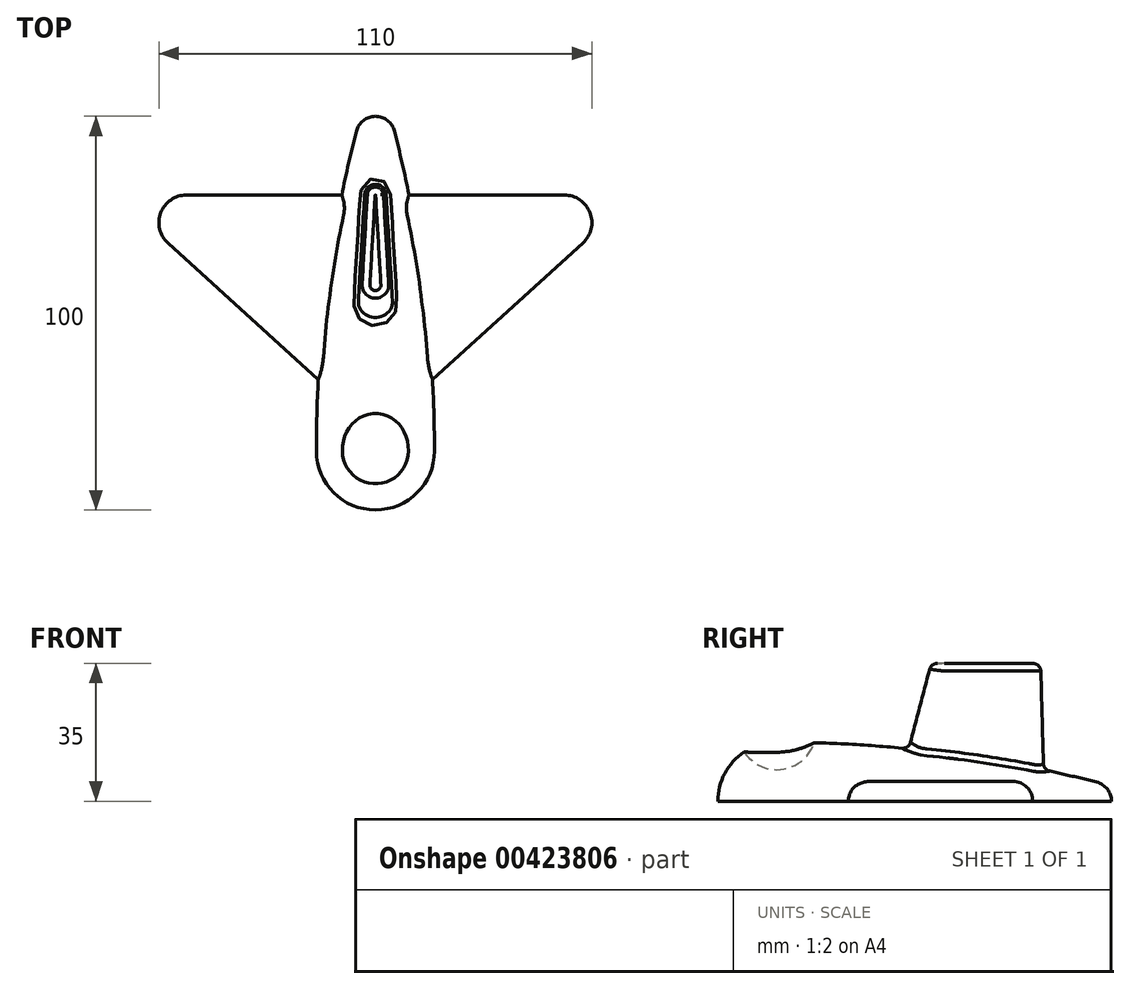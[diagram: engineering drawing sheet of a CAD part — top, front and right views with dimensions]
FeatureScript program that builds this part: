
annotation { "Feature Type Name" : "Feature", "Feature Type Description" : "" }
export const myFeature = defineFeature(function(context is Context, id is Id, definition is map)
    precondition{}
    {
        {
            var Q0;
            Q0=qCreatedBy(makeId("Top.planeOp"),FACE);
            var sketch = newSketch(context, id + "F0", { "sketchPlane" : qUnion([Q0])});
            skArc(sketch, "E0", {"start": v(-15, 0) * mm, "mid": v(-10.6, -10.6) * mm, "end": v(0, -15) * mm});
            skArc(sketch, "E1", {"start": v(0, 85) * mm, "mid": v(-3.07, 83.95) * mm, "end": v(-4.85, 81.23) * mm});
            skLineSegment(sketch, "E2", {"start": v(0, 0) * mm, "end": v(0, 80) * mm});
            skArc(sketch, "E3", {"start": v(-4.85, 81.23) * mm, "mid": v(-12.45, 40.93) * mm, "end": v(-15, 0) * mm});
            skLineSegment(sketch, "E4", {"start": v(0, -15) * mm, "end": v(0, 0) * mm});
            skLineSegment(sketch, "E5.trimOffspring", {"start": v(0, 80) * mm, "end": v(0, 85) * mm});
            skSolve(sketch);
        }
        {
            var Q0;
            Q0=makeQuery(id+"F0.imprint","IMPRINT",FACE,{"disambiguationData":[TD([[makeQuery(id+"F0.imprint","IMPRINT",EDGE,{"derivedFrom":sQuery(id+"F0.wireOp",EDGE,"E0")}),1.0]])]});
            var Q1;
            Q1=sQuery(id+"F0.wireOp",EDGE,"E2");
            revolve(context, id + "F1", {"entities" : qUnion([Q0]), "axis" : qUnion([Q1]), "revolveType" : RevolveType.ONE_DIRECTION, "angle" : 180 * degree});
        }
        {
            var Q0;
            Q0=qCreatedBy(makeId("Right.planeOp"),FACE);
            var sketch = newSketch(context, id + "F2", { "sketchPlane" : qUnion([Q0])});
            skArc(sketch, "E6", {"start": v(-9.34, 14.42) * mm, "mid": v(3.7, 8.71) * mm, "end": v(9.24, 21.83) * mm});
            skLineSegment(sketch, "E7", {"start": v(-9.34, 14.42) * mm, "end": v(9.24, 21.83) * mm});
            skSolve(sketch);
        }
        {
            var Q0;
            Q0 = qSketchRegion(id + "F2", true);
            var Q1;
            Q1=sQuery(id+"F2.wireOp",EDGE,"E7");
            revolve(context, id + "F3", {"operationType" : NewBodyOperationType.REMOVE, "entities" : qUnion([Q0]), "axis" : qUnion([Q1]), "revolveType" : RevolveType.FULL, "oppositeDirection" : true});
        }
        {
            var Q0;
            Q0=qCreatedBy(makeId("Top.planeOp"),FACE);
            var sketch = newSketch(context, id + "F4", { "sketchPlane" : qUnion([Q0])});
            skLineSegment(sketch, "E8", {"start": v(0, 5) * mm, "end": v(0, 65) * mm});
            skLineSegment(sketch, "E9", {"start": v(0, 65) * mm, "end": v(-48, 65) * mm});
            skLineSegment(sketch, "E10", {"start": v(-52.7, 52.82) * mm, "end": v(0, 5) * mm});
            skPoint(sketch, "E11.visualSharp", {"position": v(-66.13, 65) * mm});
            skArc(sketch, "E11.filletArc", {"start": v(-48, 65) * mm, "mid": v(-54.53, 60.52) * mm, "end": v(-52.7, 52.82) * mm});
            skSolve(sketch);
        }
        {
            var Q0;
            Q0=makeQuery(id+"F4.imprint","IMPRINT",FACE,{"disambiguationData":[TD([[makeQuery(id+"F4.imprint","IMPRINT",EDGE,{"derivedFrom":sQuery(id+"F4.wireOp",EDGE,"E8")}),1.0]])]});
            extrude(context, id + "F5", {"entities" : qUnion([Q0]), "depth" : 5 * mm});
        }
        {
            var Q0;
            Q0=makeQuery(id+"F5.opExtrude","CAP_FACE",FACE,{"disambiguationData":[OSD([sQuery(id+"F4.wireOp",EDGE,"E8"),sQuery(id+"F4.wireOp",EDGE,"E9"),sQuery(id+"F4.wireOp",EDGE,"E10"),sQuery(id+"F4.wireOp",EDGE,"E11.filletArc")])],"isStart":false});
            fillet(context, id + "F6", {"entities" : qUnion([Q0]), "radius" : 5 * mm, "tangentPropagation" : true, "allowEdgeOverflow" : false});
        }
        {
            var Q0;
            Q0=makeQuery(id+"F5.opExtrude","SWEPT_BODY",BODY,{"disambiguationData":[OSD([sQuery(id+"F4.wireOp",EDGE,"E8"),sQuery(id+"F4.wireOp",EDGE,"E9"),sQuery(id+"F4.wireOp",EDGE,"E10"),sQuery(id+"F4.wireOp",EDGE,"E11.filletArc")])]});
            var Q1;
            Q1=qCreatedBy(makeId("Right.planeOp"),FACE);
            mirror(context, id + "F7", {"operationType" : NewBodyOperationType.ADD, "entities" : qUnion([Q0]), "mirrorPlane" : qUnion([Q1])});
        }
        {
            var Q0;
            Q0=qCreatedBy(makeId("Top.planeOp"),FACE);
            var sketch = newSketch(context, id + "F8", { "sketchPlane" : qUnion([Q0])});
            skArc(sketch, "E12", {"start": v(3, 65.2) * mm, "mid": v(0, 68) * mm, "end": v(-3, 65.2) * mm});
            skArc(sketch, "E13", {"start": v(-4.99, 35.33) * mm, "mid": v(0, 30) * mm, "end": v(4.99, 35.33) * mm});
            skLineSegment(sketch, "E14", {"start": v(3, 65.2) * mm, "end": v(4.99, 35.33) * mm});
            skLineSegment(sketch, "E15.MirrorCS", {"start": v(-3, 65.2) * mm, "end": v(-4.99, 35.33) * mm});
            skSolve(sketch);
        }
        {
            var Q0;
            Q0=qCreatedBy(makeId("Top.planeOp"),FACE);
            cPlane(context, id + "F9", {"entities" : qUnion([Q0]), "cplaneType" : CPlaneType.OFFSET, "offset" : 35 * mm, "width" : 150 * mm, "height" : 150 * mm});
        }
        {
            var Q0;
            Q0=qCreatedBy(id+"F9.planeOp",FACE);
            var sketch = newSketch(context, id + "F10", { "sketchPlane" : qUnion([Q0])});
            skArc(sketch, "E16", {"start": v(-3.3, 42.7) * mm, "mid": v(0, 39.2) * mm, "end": v(3.3, 42.7) * mm});
            skArc(sketch, "E17", {"start": v(2, 65.12) * mm, "mid": v(0, 67) * mm, "end": v(-2, 65.12) * mm});
            skLineSegment(sketch, "E18", {"start": v(2, 65.12) * mm, "end": v(3.3, 42.7) * mm});
            skLineSegment(sketch, "E19.MirrorCS", {"start": v(-2, 65.12) * mm, "end": v(-3.3, 42.7) * mm});
            skSolve(sketch);
        }
        {
            var Q1;
            Q1 = qSketchRegion(id + "F8", true);
            var Q2;
            Q2=makeQuery(id+"F10.imprint","IMPRINT",FACE,{"disambiguationData":[TD([[makeQuery(id+"F10.imprint","IMPRINT",EDGE,{"derivedFrom":sQuery(id+"F10.wireOp",EDGE,"E16")}),1.0]])]});
            loft(context, id + "F11", {"operationType" : NewBodyOperationType.ADD, "sheetProfilesArray" : [{ "sheetProfileEntities" : qUnion([Q1]) }, { "sheetProfileEntities" : qUnion([Q2]) }]});
        }
        {
            var Q0;
            Q0=makeQuery(id+"F11.opLoft","CAP_FACE",FACE,{"disambiguationData":[OSD([makeQuery(id+"F10.imprint","IMPRINT",FACE,{"disambiguationData":[TD([[makeQuery(id+"F10.imprint","IMPRINT",EDGE,{"derivedFrom":sQuery(id+"F10.wireOp",EDGE,"E16")}),1.0]])]})])],"isStart":true});
            fillet(context, id + "F12", {"entities" : qUnion([Q0]), "radius" : 2 * mm, "tangentPropagation" : true, "allowEdgeOverflow" : false});
        }
        {
            var Q0;
            Q0=makeQuery(id+"F11.boolean.opBoolean","INTERSECT",EDGE,{"derivedFrom":[makeQuery(id+"F1.opRevolve","SWEPT_FACE",FACE,{"disambiguationData":[OSD([sQuery(id+"F0.wireOp",EDGE,"E3")])]}),makeQuery(id+"F11.opLoft","SWEPT_FACE",FACE,{"disambiguationData":[OSD([sQuery(id+"F8.wireOp",EDGE,"E12"),sQuery(id+"F8.wireOp",EDGE,"E14"),sQuery(id+"F8.wireOp",EDGE,"E15.MirrorCS"),sQuery(id+"F10.wireOp",EDGE,"E17"),sQuery(id+"F10.wireOp",EDGE,"E18"),sQuery(id+"F10.wireOp",EDGE,"E19.MirrorCS")])]})]});
            fillet(context, id + "F13", {"entities" : qUnion([Q0]), "radius" : 2 * mm, "tangentPropagation" : true, "allowEdgeOverflow" : false});
        }
    });
